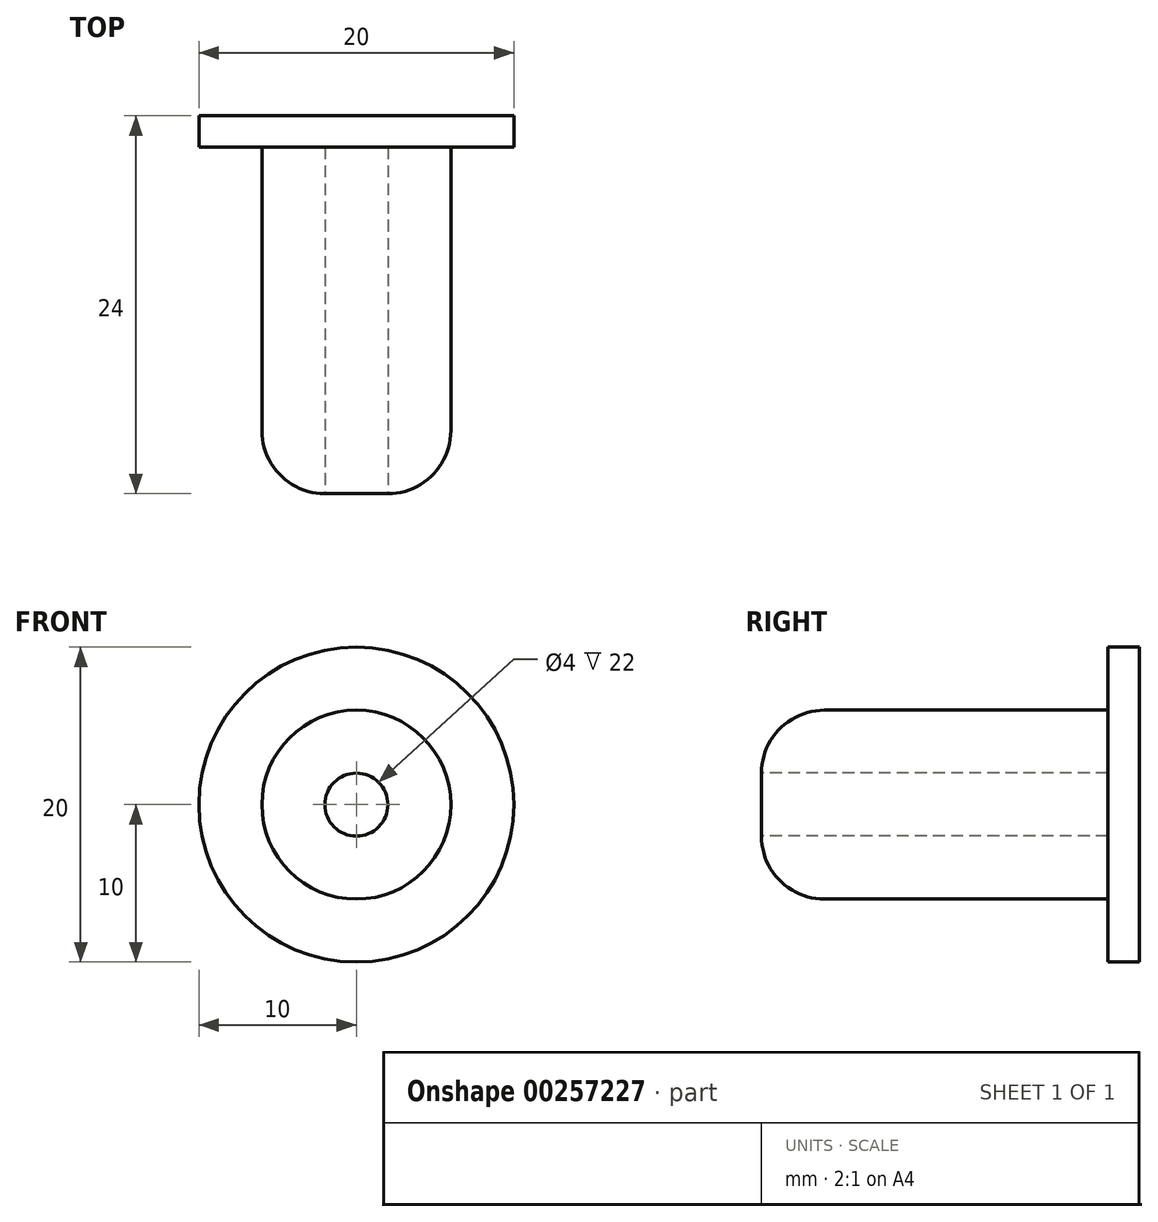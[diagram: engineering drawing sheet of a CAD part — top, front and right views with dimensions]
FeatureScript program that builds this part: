
annotation { "Feature Type Name" : "Feature", "Feature Type Description" : "" }
export const myFeature = defineFeature(function(context is Context, id is Id, definition is map)
    precondition{}
    {
        {
            var Q0;
            Q0=qCreatedBy(makeId("Front.planeOp"),FACE);
            var sketch = newSketch(context, id + "F0", { "sketchPlane" : qUnion([Q0])});
            skCircle(sketch, "E0", {"center": v(0, 0) * mm, "radius": 6 * mm});
            skCircle(sketch, "E1.0", {"center": v(0, 0) * mm, "radius": 10 * mm});
            skSolve(sketch);
        }
        {
            var Q0;
            Q0=makeQuery(id+"F0.imprint","IMPRINT",FACE,{"disambiguationData":[TD([[makeQuery(id+"F0.imprint","IMPRINT",EDGE,{"derivedFrom":sQuery(id+"F0.wireOp",EDGE,"E0")}),1.0]])]});
            extrude(context, id + "F1", {"entities" : qUnion([Q0]), "depth" : 24 * mm});
        }
        {
            var Q0;
            Q0 = qSketchRegion(id + "F0", true);
            extrude(context, id + "F2", {"entities" : qUnion([Q0]), "operationType" : NewBodyOperationType.ADD, "depth" : 2 * mm});
        }
        {
            var Q0;
            Q0=makeQuery(id+"F1.opExtrude","CAP_EDGE",EDGE,{"disambiguationData":[OSD([sQuery(id+"F0.wireOp",EDGE,"E0")])],"isStart":false});
            fillet(context, id + "F3", {"entities" : qUnion([Q0]), "radius" : 4 * mm, "tangentPropagation" : true, "allowEdgeOverflow" : false});
        }
        {
            var Q0;
            Q0=makeQuery(id+"F1.opExtrude","CAP_FACE",FACE,{"disambiguationData":[OSD([sQuery(id+"F0.wireOp",EDGE,"E0")])],"isStart":false});
            extrude(context, id + "F4", {"entities" : qUnion([Q0]), "operationType" : NewBodyOperationType.REMOVE, "oppositeDirection" : true, "depth" : 22 * mm});
        }
    });
